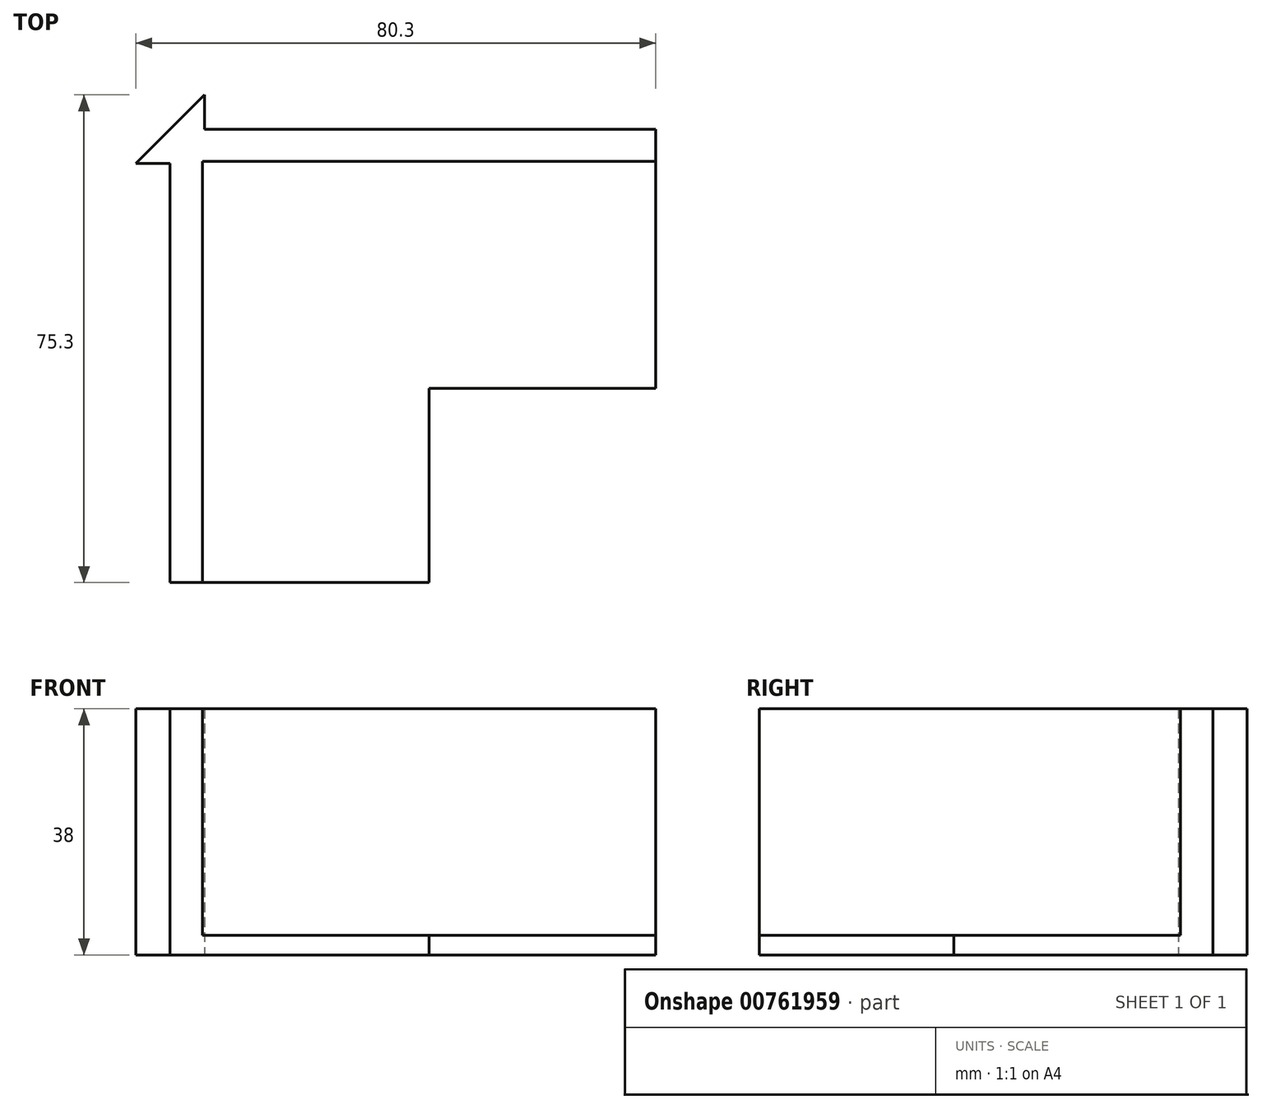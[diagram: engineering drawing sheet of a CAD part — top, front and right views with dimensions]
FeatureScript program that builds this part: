
annotation { "Feature Type Name" : "Feature", "Feature Type Description" : "" }
export const myFeature = defineFeature(function(context is Context, id is Id, definition is map)
    precondition{}
    {
        {
            var Q0;
            Q0=qCreatedBy(makeId("Front.planeOp"),FACE);
            var sketch = newSketch(context, id + "F0", { "sketchPlane" : qUnion([Q0])});
            skLineSegment(sketch, "E0", {"start": v(-60, 38) * mm, "end": v(-60, 0) * mm});
            skLineSegment(sketch, "E1", {"start": v(-60, 0) * mm, "end": v(-20, 0) * mm});
            skLineSegment(sketch, "E2", {"start": v(-20, 0) * mm, "end": v(-20, 3) * mm});
            skLineSegment(sketch, "E3", {"start": v(-20, 3) * mm, "end": v(-55, 3) * mm});
            skLineSegment(sketch, "E4", {"start": v(-55, 3) * mm, "end": v(-55, 38) * mm});
            skLineSegment(sketch, "E5", {"start": v(-55, 38) * mm, "end": v(-60, 38) * mm});
            skSolve(sketch);
        }
        {
            var Q0;
            Q0=makeQuery(id+"F0.imprint","IMPRINT",FACE,{"disambiguationData":[TD([[makeQuery(id+"F0.imprint","IMPRINT",EDGE,{"derivedFrom":sQuery(id+"F0.wireOp",EDGE,"E0")}),1.0]])]});
            extrude(context, id + "F1", {"entities" : qUnion([Q0]), "depth" : 70 * mm, "offsetDistance" : 25 * mm});
        }
        {
            var Q0;
            Q0=makeQuery(id+"F1.opExtrude","SWEPT_FACE",FACE,{"disambiguationData":[OSD([sQuery(id+"F0.wireOp",EDGE,"E4")])]});
            var sketch = newSketch(context, id + "F2", { "sketchPlane" : qUnion([Q0])});
            skLineSegment(sketch, "E6", {"start": v(0, 0) * mm, "end": v(-40, 0) * mm});
            skLineSegment(sketch, "E7", {"start": v(-40, 0) * mm, "end": v(-40, 3) * mm});
            skLineSegment(sketch, "E8", {"start": v(-40, 3) * mm, "end": v(-5, 3) * mm});
            skLineSegment(sketch, "E9", {"start": v(-5, 3) * mm, "end": v(-5, 38) * mm});
            skLineSegment(sketch, "E10", {"start": v(-5, 38) * mm, "end": v(0, 38) * mm});
            skLineSegment(sketch, "E11", {"start": v(0, 38) * mm, "end": v(0, 0) * mm});
            skSolve(sketch);
        }
        {
            var Q0;
            {var subQ0=sQuery(id+"F2.wireOp",EDGE,"E9");Q0=makeQuery(id+"F2.imprint","IMPRINT",FACE,{"disambiguationData":[TD([[makeQuery(id+"F2.imprint","IMPRINT",EDGE,{"derivedFrom":subQ0}),-1.0]])]});}
            var Q1;
            {var subQ4=sQuery(id+"F2.wireOp",EDGE,"E6");Q1=makeQuery(id+"F2.imprint","IMPRINT",FACE,{"disambiguationData":[TD([[makeQuery(id+"F2.imprint","IMPRINT",EDGE,{"derivedFrom":subQ4}),-1.0]])]});}
            extrude(context, id + "F3", {"entities" : qUnion([Q0, Q1]), "depth" : 70 * mm, "offsetDistance" : 25 * mm});
        }
        {
            var Q0;
            Q0=makeQuery(id+"F1.opExtrude","SWEPT_BODY",BODY,{"disambiguationData":[OSD([sQuery(id+"F0.wireOp",EDGE,"E0"),sQuery(id+"F0.wireOp",EDGE,"E1"),sQuery(id+"F0.wireOp",EDGE,"E2"),sQuery(id+"F0.wireOp",EDGE,"E3"),sQuery(id+"F0.wireOp",EDGE,"E4"),sQuery(id+"F0.wireOp",EDGE,"E5")])]});
            var Q1;
            Q1=makeQuery(id+"F3.opExtrude","SWEPT_BODY",BODY,{"disambiguationData":[OSD([sQuery(id+"F2.wireOp",EDGE,"E6"),sQuery(id+"F2.wireOp",EDGE,"E7"),sQuery(id+"F2.wireOp",EDGE,"E8"),sQuery(id+"F2.wireOp",EDGE,"E9"),sQuery(id+"F2.wireOp",EDGE,"E10"),sQuery(id+"F2.wireOp",EDGE,"E11")])]});
            booleanBodies(context, id + "F4", {"operationType" : BooleanOperationType.UNION, "tools" : qUnion([Q0, Q1])});
        }
        {
            var Q0;
            Q0=makeQuery(id+"F4.opBoolean","MERGE",FACE,{"derivedFrom":[makeQuery(id+"F1.opExtrude","SWEPT_FACE",FACE,{"disambiguationData":[OSD([sQuery(id+"F0.wireOp",EDGE,"E1")])]}),makeQuery(id+"F3.opExtrude","SWEPT_FACE",FACE,{"disambiguationData":[OSD([sQuery(id+"F2.wireOp",EDGE,"E6")])]})]});
            var sketch = newSketch(context, id + "F5", { "sketchPlane" : qUnion([Q0])});
            skLineSegment(sketch, "E12", {"start": v(-65.3, 5.3) * mm, "end": v(-54.7, -5.3) * mm});
            skLineSegment(sketch, "E13", {"start": v(-65.3, 5.3) * mm, "end": v(-60, 5.3) * mm});
            skLineSegment(sketch, "E14", {"start": v(-60, 5.3) * mm, "end": v(-60, 0) * mm});
            skLineSegment(sketch, "E15", {"start": v(-60, 0) * mm, "end": v(-54.7, 0) * mm});
            skLineSegment(sketch, "E16", {"start": v(-54.7, 0) * mm, "end": v(-54.7, -5.3) * mm});
            skSolve(sketch);
        }
        {
            var Q0;
            {var subQ2=sQuery(id+"F5.wireOp",EDGE,"E13");Q0=makeQuery(id+"F5.imprint","IMPRINT",FACE,{"disambiguationData":[TD([[makeQuery(id+"F5.imprint","IMPRINT",EDGE,{"derivedFrom":subQ2}),-1.0]])]});}
            var Q1;
            {var subQ0=sQuery(id+"F5.wireOp",EDGE,"E15");Q1=makeQuery(id+"F5.imprint","IMPRINT",FACE,{"disambiguationData":[TD([[makeQuery(id+"F5.imprint","IMPRINT",EDGE,{"derivedFrom":subQ0}),-1.0]])]});}
            var Q2;
            Q2=makeQuery(id+"F4.opBoolean","MERGE",FACE,{"derivedFrom":[makeQuery(id+"F1.opExtrude","SWEPT_FACE",FACE,{"disambiguationData":[OSD([sQuery(id+"F0.wireOp",EDGE,"E5")])]}),makeQuery(id+"F3.opExtrude","SWEPT_FACE",FACE,{"disambiguationData":[OSD([sQuery(id+"F2.wireOp",EDGE,"E10")])]})]});
            extrude(context, id + "F6", {"entities" : qUnion([Q0, Q1]), "operationType" : NewBodyOperationType.ADD, "endBound" : BoundingType.UP_TO_SURFACE, "oppositeDirection" : true, "depth" : 25 * mm, "endBoundEntityFace" : qUnion([Q2]), "offsetDistance" : 25 * mm});
        }
    });
